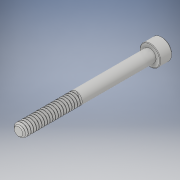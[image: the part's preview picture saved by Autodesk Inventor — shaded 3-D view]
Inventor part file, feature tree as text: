
AUTODESK INVENTOR PART (.ipt)
format: ipt  version: 2018 (Build 220112000, 112)  size: 742,400 bytes
history: native  units: in
note: dims shown in document units (in); Inventor stores cm internally (conversion verified against a paired STEP export)
features: chamfer x1
ambient origin geometry x8: Origin, YZ Plane, XZ Plane, XY Plane, X Axis, Y Axis, Z Axis, Center Point
bodies: Solid1 (feature_tree)
feature tree (1):
  chamfer  "Chamfer2"  [1 undecoded]
note: 1 required parameter value undecoded (feature->parameter linkage not recoverable at this tier; creation-order binding heuristic only, values carry confidence <= 0.55)
